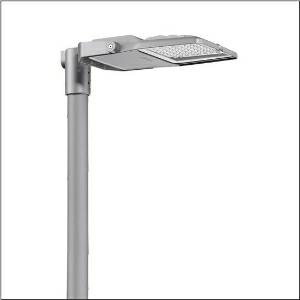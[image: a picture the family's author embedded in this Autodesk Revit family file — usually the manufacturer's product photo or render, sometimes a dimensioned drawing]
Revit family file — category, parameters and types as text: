
# Revit family: floodlight_fl_21_mini___pl61_5xa7776c4c3a_c7e0
name_source: partatom
category: Lighting Fixtures
units: mm (PartAtom-declared; Revit-internal decimal feet)

## family parameters
Cut with Voids When Loaded = No
Host = Face
Light Source = No
Part Type = Normal
Room Calculation Point = No
Round Connector Dimension = Use Diameter
Shared = No

## types (1)
- --- (1 x LED, 12460 lm, 89 W, 4000K)
    Apparent Load = 89 VA
    CIE Flux Codes = 33 65 98 100 100
    Color Rendering = 70
    Color Temperature = 4000K
    Default Elevation = 1800 mm
    Description = Floodlight FL 21 mini, floodlight, primary light control with lens, of PMMA, primary optical cover: protective disc, of toughened safety glass, transparent, light distribution: PL61, light emission: direct distribution, installation type: surface-mounted, LED, High Power LED, rated luminous flux: 12.460lm, luminous efficacy: 140lm/W, light colour: 740, colour temperature: 4000K, control gear: D4iSmart Interface (Zhaga), control: overheat protection, constant luminous flux control, time-dependent luminous flux control, flexible luminous flux parameterisation, pre-setting: logarithmic dimming characteristic, with terminal, 6-pole, mains connection: 220..240V, AC, 50/60Hz, start of lifetime: 89W, end of service life: 94W, reduction: 43W, mast bracket, of diecast aluminium, powder-coated, Siteco® metallic grey (DB 702S), corrosivity category C5 mid according to DIN EN ISO 12944, suitable for swimming pools, chlorine-resistant, sealing non-destructively replaceable, mast bracket, of steel, galvanised, powder-coated, Siteco® metallic grey (DB 702S), Smart Interface below and above, protection rating (complete): IP66, insulation class (complete): insulation class II (safety insulation), certification: CE, ENEC, VDE, protection symbol: D, impact resistance: IK08, permissible operating ambient temperature: -40..+40°C, permissible operating ambient temperature for outdoor applications: -40..+50°C, standard: DIN EN 12944, LABS conformity tested according to VDMA 24364:2018-05, packaging unit: 1 piece

Light Distribution: PL61
    Height = 70 mm
    Lamp = 1 x LED
    Lamp Light Flux = 12460 lm
    Lamp Power = 89 W
    Lamp count = 1
    Length = 485 mm
    Luminous efficacy = 140 lm/W
    Manufacturer = Siteco
    ModVariant = No
    Model = 5XA7776C4C3A
    Number of Poles = 1
    OnlyDefault = Yes
    Power Factor = 1
    Product Name = Floodlight FL 21 mini | PL61
    Product group = floodlight | pylon annexe
    ProductGroupID = 6201
    Protection Class = Protection class II
    Protection Degree = IP 66
    RLX_Detail_Level = 1
    RLX_Emergency_Light_Flux = 0 lm
    RLX_Emergency_Type = 0
    RLX_Emergency_Type_DB = No
    RlxData = <blob elided: 100933 chars, md5=3afa1723>
    Socket = socket
    Standby Power = 0 W
    System Light Flux = 12460 lm
    System Power = 89 W
    Type Comments = factory setting: luminous flux: 100 % | dim-lin: 254 | 456 mA
    Type Image = l_1007125.jpg
    URL = http://relux.com
    VarID = @adj_121937
    Voltage = 0 V
    Weight = 0.00 kg
    Width = 337 mm

## geometry (parser evidence)
native form markers: Blend x4, Sweep x14
no freeform markers — native parametric forms only
